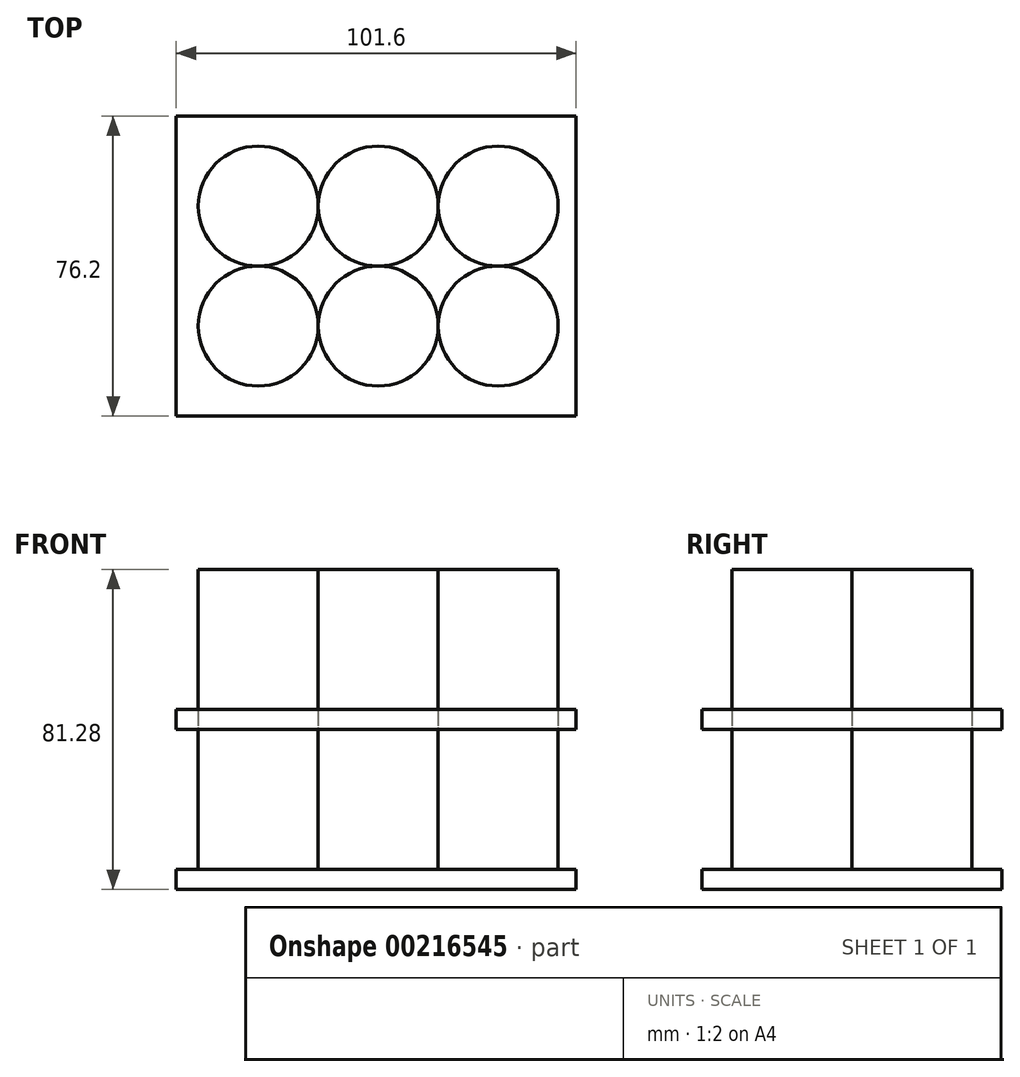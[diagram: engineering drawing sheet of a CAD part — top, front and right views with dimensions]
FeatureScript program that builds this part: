
annotation { "Feature Type Name" : "Feature", "Feature Type Description" : "" }
export const myFeature = defineFeature(function(context is Context, id is Id, definition is map)
    precondition{}
    {
        {
            var Q0;
            Q0=qCreatedBy(makeId("Top.planeOp"),FACE);
            var sketch = newSketch(context, id + "F0", { "sketchPlane" : qUnion([Q0])});
            skCircle(sketch, "E0", {"center": v(-29.97, -15.25) * mm, "radius": 15.24 * mm});
            skCircle(sketch, "E1", {"center": v(0.51, -15.25) * mm, "radius": 15.24 * mm});
            skCircle(sketch, "E2", {"center": v(31, -15.25) * mm, "radius": 15.24 * mm});
            skLineSegment(sketch, "E3", {"start": v(-29.97, -15.25) * mm, "end": v(50.03, -15.25) * mm, "construction": true});
            skCircle(sketch, "E4", {"center": v(-29.97, 15.23) * mm, "radius": 15.24 * mm});
            skCircle(sketch, "E5", {"center": v(0.51, 15.23) * mm, "radius": 15.24 * mm});
            skCircle(sketch, "E6", {"center": v(31, 15.23) * mm, "radius": 15.24 * mm});
            skLineSegment(sketch, "E7", {"start": v(-29.97, 15.23) * mm, "end": v(34.43, 15.23) * mm, "construction": true});
            skLineSegment(sketch, "E8", {"start": v(-29.97, 15.23) * mm, "end": v(-29.97, -15.25) * mm, "construction": true});
            skSolve(sketch);
        }
        {
            var Q0;
            {var subQ0=sQuery(id+"F0.wireOp",EDGE,"ICpDPUjX-ivMe-23Ei-ieje-qIsjfVPonkm3");var subQ1=makeQuery(id+"F0.imprint","INTERSECT",VERTEX,{"derivedFrom":[subQ0,sQuery(id+"F0.wireOp",EDGE,"1585de0c-b4fc-4455-9636-1ccd38715f07")]});Q0=makeQuery(id+"F0.imprint","IMPRINT",FACE,{"disambiguationData":[TD([[makeQuery(id+"F0.imprint","IMPRINT",EDGE,{"disambiguationData":[TD([[subQ1,-1.0]])],"derivedFrom":subQ0}),1.0]])]});}
            var Q1;
            {var subQ0=sQuery(id+"F0.wireOp",EDGE,"1585de0c-b4fc-4455-9636-1ccd38715f07");var subQ1=makeQuery(id+"F0.imprint","INTERSECT",VERTEX,{"derivedFrom":[sQuery(id+"F0.wireOp",EDGE,"ICpDPUjX-ivMe-23Ei-ieje-qIsjfVPonkm3"),subQ0]});Q1=makeQuery(id+"F0.imprint","IMPRINT",FACE,{"disambiguationData":[TD([[makeQuery(id+"F0.imprint","IMPRINT",EDGE,{"disambiguationData":[TD([[subQ1,1.0]])],"derivedFrom":subQ0}),1.0]])]});}
            var Q2;
            {var subQ0=sQuery(id+"F0.wireOp",EDGE,"8cf919d0-c88a-4376-973f-18324e1bfcb2");var subQ1=makeQuery(id+"F0.imprint","INTERSECT",VERTEX,{"derivedFrom":[sQuery(id+"F0.wireOp",EDGE,"1585de0c-b4fc-4455-9636-1ccd38715f07"),subQ0]});Q2=makeQuery(id+"F0.imprint","IMPRINT",FACE,{"disambiguationData":[TD([[makeQuery(id+"F0.imprint","IMPRINT",EDGE,{"disambiguationData":[TD([[subQ1,-1.0]])],"derivedFrom":subQ0}),1.0]])]});}
            var Q3;
            {var subQ0=sQuery(id+"F0.wireOp",EDGE,"0c448a11-c32a-4d7b-bc3d-f4b18554e8e6");var subQ1=makeQuery(id+"F0.imprint","INTERSECT",VERTEX,{"derivedFrom":[sQuery(id+"F0.wireOp",EDGE,"8cf919d0-c88a-4376-973f-18324e1bfcb2"),subQ0]});Q3=makeQuery(id+"F0.imprint","IMPRINT",FACE,{"disambiguationData":[TD([[makeQuery(id+"F0.imprint","IMPRINT",EDGE,{"disambiguationData":[TD([[subQ1,-1.0]])],"derivedFrom":subQ0}),1.0]])]});}
            var Q4;
            {var subQ0=sQuery(id+"F0.wireOp",EDGE,"877ee094-fdc9-495d-ab0e-c5a52c05f9cd");var subQ4=makeQuery(id+"F0.imprint","INTERSECT",VERTEX,{"derivedFrom":[sQuery(id+"F0.wireOp",EDGE,"8cf919d0-c88a-4376-973f-18324e1bfcb2"),subQ0]});Q4=makeQuery(id+"F0.imprint","IMPRINT",FACE,{"disambiguationData":[TD([[makeQuery(id+"F0.imprint","IMPRINT",EDGE,{"disambiguationData":[TD([[subQ4,1.0]])],"derivedFrom":subQ0}),1.0]])]});}
            var Q5;
            {var subQ0=sQuery(id+"F0.wireOp",EDGE,"d8245553-00ec-417b-91d8-0db8256ae251");var subQ4=makeQuery(id+"F0.imprint","INTERSECT",VERTEX,{"derivedFrom":[sQuery(id+"F0.wireOp",EDGE,"1585de0c-b4fc-4455-9636-1ccd38715f07"),subQ0]});Q5=makeQuery(id+"F0.imprint","IMPRINT",FACE,{"disambiguationData":[TD([[makeQuery(id+"F0.imprint","IMPRINT",EDGE,{"disambiguationData":[TD([[subQ4,1.0]])],"derivedFrom":subQ0}),1.0]])]});}
            var Q6;
            {var subQ0=sQuery(id+"F0.wireOp",EDGE,"E0");var subQ1=makeQuery(id+"F0.imprint","INTERSECT",VERTEX,{"derivedFrom":[sQuery(id+"F0.wireOp",EDGE,"d8245553-00ec-417b-91d8-0db8256ae251"),subQ0]});Q6=makeQuery(id+"F0.imprint","IMPRINT",FACE,{"disambiguationData":[TD([[makeQuery(id+"F0.imprint","IMPRINT",EDGE,{"disambiguationData":[TD([[subQ1,1.0]])],"derivedFrom":subQ0}),1.0]])]});}
            var Q7;
            {var subQ0=sQuery(id+"F0.wireOp",EDGE,"E1");var subQ1=makeQuery(id+"F0.imprint","INTERSECT",VERTEX,{"derivedFrom":[subQ0,sQuery(id+"F0.wireOp",EDGE,"E2")]});Q7=makeQuery(id+"F0.imprint","IMPRINT",FACE,{"disambiguationData":[TD([[makeQuery(id+"F0.imprint","IMPRINT",EDGE,{"disambiguationData":[TD([[subQ1,-1.0]])],"derivedFrom":subQ0}),1.0]])]});}
            var Q8;
            {var subQ0=sQuery(id+"F0.wireOp",EDGE,"E2");var subQ1=makeQuery(id+"F0.imprint","INTERSECT",VERTEX,{"derivedFrom":[sQuery(id+"F0.wireOp",EDGE,"0c448a11-c32a-4d7b-bc3d-f4b18554e8e6"),subQ0]});Q8=makeQuery(id+"F0.imprint","IMPRINT",FACE,{"disambiguationData":[TD([[makeQuery(id+"F0.imprint","IMPRINT",EDGE,{"disambiguationData":[TD([[subQ1,-1.0]])],"derivedFrom":subQ0}),1.0]])]});}
            var Q9;
            {var subQ0=sQuery(id+"F0.wireOp",EDGE,"E4");var subQ1=makeQuery(id+"F0.imprint","INTERSECT",VERTEX,{"derivedFrom":[sQuery(id+"F0.wireOp",EDGE,"E0"),subQ0]});Q9=makeQuery(id+"F0.imprint","IMPRINT",FACE,{"disambiguationData":[TD([[makeQuery(id+"F0.imprint","IMPRINT",EDGE,{"disambiguationData":[TD([[subQ1,1.0]])],"derivedFrom":subQ0}),1.0]])]});}
            var Q10;
            {var subQ0=sQuery(id+"F0.wireOp",EDGE,"E5");var subQ1=makeQuery(id+"F0.imprint","INTERSECT",VERTEX,{"derivedFrom":[sQuery(id+"F0.wireOp",EDGE,"E4"),subQ0]});Q10=makeQuery(id+"F0.imprint","IMPRINT",FACE,{"disambiguationData":[TD([[makeQuery(id+"F0.imprint","IMPRINT",EDGE,{"disambiguationData":[TD([[subQ1,1.0]])],"derivedFrom":subQ0}),1.0]])]});}
            var Q11;
            {var subQ0=sQuery(id+"F0.wireOp",EDGE,"E6");var subQ1=makeQuery(id+"F0.imprint","INTERSECT",VERTEX,{"derivedFrom":[sQuery(id+"F0.wireOp",EDGE,"E2"),subQ0]});Q11=makeQuery(id+"F0.imprint","IMPRINT",FACE,{"disambiguationData":[TD([[makeQuery(id+"F0.imprint","IMPRINT",EDGE,{"disambiguationData":[TD([[subQ1,1.0]])],"derivedFrom":subQ0}),1.0]])]});}
            var Q12;
            Q12=sQuery(id+"F0.wireOp",EDGE,"877ee094-fdc9-495d-ab0e-c5a52c05f9cd");
            var Q13;
            Q13=sQuery(id+"F0.wireOp",EDGE,"ICpDPUjX-ivMe-23Ei-ieje-qIsjfVPonkm3");
            var Q14;
            Q14=sQuery(id+"F0.wireOp",EDGE,"E2");
            var Q15;
            Q15=sQuery(id+"F0.wireOp",EDGE,"E1");
            var Q16;
            Q16=sQuery(id+"F0.wireOp",EDGE,"E0");
            var Q17;
            Q17=sQuery(id+"F0.wireOp",EDGE,"0c448a11-c32a-4d7b-bc3d-f4b18554e8e6");
            var Q18;
            Q18=sQuery(id+"F0.wireOp",EDGE,"d8245553-00ec-417b-91d8-0db8256ae251");
            var Q19;
            Q19=sQuery(id+"F0.wireOp",EDGE,"8cf919d0-c88a-4376-973f-18324e1bfcb2");
            var Q20;
            Q20=sQuery(id+"F0.wireOp",EDGE,"1585de0c-b4fc-4455-9636-1ccd38715f07");
            extrude(context, id + "F1", {"entities" : qUnion([Q0, Q1, Q2, Q3, Q4, Q5, Q6, Q7, Q8, Q9, Q10, Q11]), "surfaceEntities" : qUnion([Q12, Q13, Q14, Q15, Q16, Q17, Q18, Q19, Q20]), "depth" : 76.2 * mm});
        }
        {
            var Q0;
            Q0=qCreatedBy(makeId("Front.planeOp"),FACE);
            var sketch = newSketch(context, id + "F2", { "sketchPlane" : qUnion([Q0])});
            skLineSegment(sketch, "E9.bottom", {"start": v(50.8, 0) * mm, "end": v(-50.8, 0) * mm});
            skLineSegment(sketch, "E9.top", {"start": v(50.8, -5.08) * mm, "end": v(-50.8, -5.08) * mm});
            skLineSegment(sketch, "E9.left", {"start": v(50.8, 0) * mm, "end": v(50.8, -5.08) * mm});
            skLineSegment(sketch, "E9.right", {"start": v(-50.8, 0) * mm, "end": v(-50.8, -5.08) * mm});
            skLineSegment(sketch, "E10", {"start": v(-45.8, 0) * mm, "end": v(-45.8, 76.2) * mm, "construction": true});
            skLineSegment(sketch, "E11", {"start": v(-45.8, 35.56) * mm, "end": v(45.84, 35.56) * mm, "construction": true});
            skLineSegment(sketch, "E12.bottom", {"start": v(50.8, 40.64) * mm, "end": v(-50.8, 40.64) * mm});
            skLineSegment(sketch, "E12.top", {"start": v(50.8, 35.56) * mm, "end": v(-50.8, 35.56) * mm});
            skLineSegment(sketch, "E12.left", {"start": v(50.8, 40.64) * mm, "end": v(50.8, 35.56) * mm});
            skLineSegment(sketch, "E12.right", {"start": v(-50.8, 40.64) * mm, "end": v(-50.8, 35.56) * mm});
            skLineSegment(sketch, "E13", {"start": v(-50.8, 40.64) * mm, "end": v(-50.8, -5.08) * mm, "construction": true});
            skSolve(sketch);
        }
        {
            var Q0;
            Q0=makeQuery(id+"F2.imprint","IMPRINT",FACE,{"disambiguationData":[TD([[makeQuery(id+"F2.imprint","IMPRINT",EDGE,{"derivedFrom":sQuery(id+"F2.wireOp",EDGE,"E9.bottom")}),1.0]])]});
            var Q1;
            Q1=makeQuery(id+"F2.imprint","IMPRINT",FACE,{"disambiguationData":[TD([[makeQuery(id+"F2.imprint","IMPRINT",EDGE,{"derivedFrom":sQuery(id+"F2.wireOp",EDGE,"E12.bottom")}),1.0]])]});
            var Q2;
            Q2=sQuery(id+"F2.wireOp",EDGE,"E9.bottom");
            extrude(context, id + "F3", {"entities" : qUnion([Q0, Q1]), "surfaceEntities" : qUnion([Q2]), "endBound" : BoundingType.SYMMETRIC, "oppositeDirection" : true, "depth" : 76.2 * mm});
        }
    });
